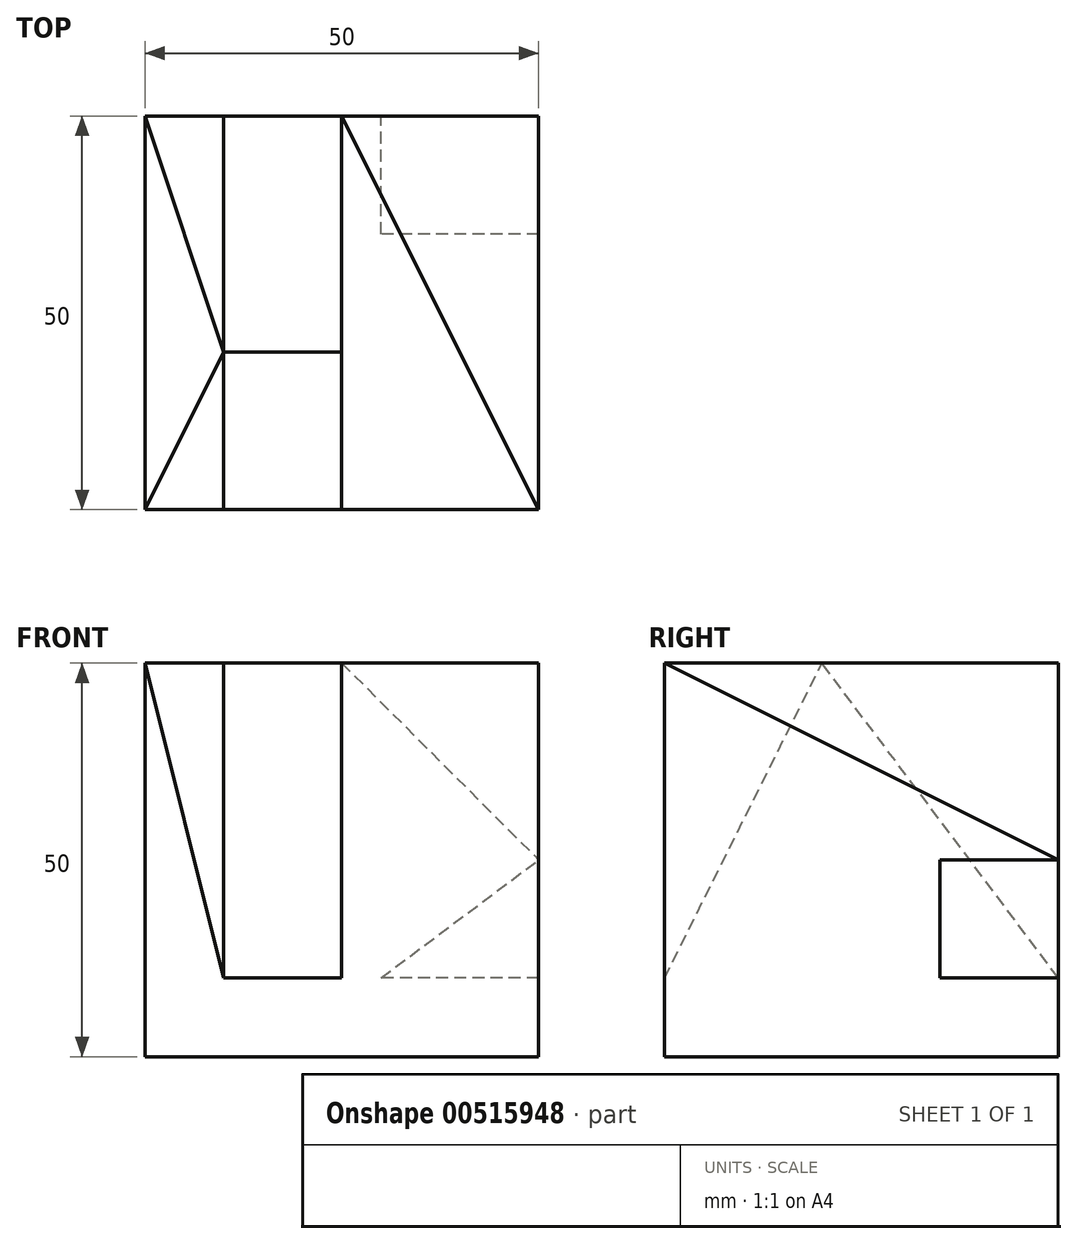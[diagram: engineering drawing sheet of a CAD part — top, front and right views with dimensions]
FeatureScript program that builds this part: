
annotation { "Feature Type Name" : "Feature", "Feature Type Description" : "" }
export const myFeature = defineFeature(function(context is Context, id is Id, definition is map)
    precondition{}
    {
        {
            var Q0;
            Q0=qCreatedBy(makeId("Top.planeOp"),FACE);
            var sketch = newSketch(context, id + "F0", { "sketchPlane" : qUnion([Q0])});
            skLineSegment(sketch, "E0.bottom", {"start": v(0, 0) * mm, "end": v(50, 0) * mm});
            skLineSegment(sketch, "E0.top", {"start": v(0, 50) * mm, "end": v(50, 50) * mm});
            skLineSegment(sketch, "E0.left", {"start": v(0, 0) * mm, "end": v(0, 50) * mm});
            skLineSegment(sketch, "E0.right", {"start": v(50, 0) * mm, "end": v(50, 50) * mm});
            skSolve(sketch);
        }
        {
            var Q0;
            Q0 = qSketchRegion(id + "F0", true);
            extrude(context, id + "F1", {"entities" : qUnion([Q0]), "depth" : 50 * mm, "offsetDistance" : 25 * mm});
        }
        {
            var Q0;
            Q0=makeQuery(id+"F1.opExtrude","CAP_FACE",FACE,{"disambiguationData":[OSD([sQuery(id+"F0.wireOp",EDGE,"E0.bottom"),sQuery(id+"F0.wireOp",EDGE,"E0.top"),sQuery(id+"F0.wireOp",EDGE,"E0.left"),sQuery(id+"F0.wireOp",EDGE,"E0.right")])],"isStart":false});
            var sketch = newSketch(context, id + "F2", { "sketchPlane" : qUnion([Q0])});
            skLineSegment(sketch, "E1", {"start": v(50, 0) * mm, "end": v(25, 50) * mm});
            skSolve(sketch);
        }
        {
            var Q0;
            Q0=makeQuery(id+"F1.opExtrude","SWEPT_FACE",FACE,{"disambiguationData":[OSD([sQuery(id+"F0.wireOp",EDGE,"E0.top")])]});
            var sketch = newSketch(context, id + "F3", { "sketchPlane" : qUnion([Q0])});
            skLineSegment(sketch, "E2", {"start": v(-25, 50) * mm, "end": v(-50, 25) * mm});
            skSolve(sketch);
        }
        {
            var Q1;
            {var subQ0=sQuery(id+"F2.wireOp",EDGE,"E1");Q1=makeQuery(id+"F2.imprint","IMPRINT",FACE,{"disambiguationData":[TD([[makeQuery(id+"F2.imprint","IMPRINT",EDGE,{"derivedFrom":subQ0}),-1.0]])]});}
            var Q2;
            Q2=sQuery(id+"F3.wireOp",VERTEX,"E2.end");
            loft(context, id + "F4", {"operationType" : NewBodyOperationType.REMOVE, "sheetProfilesArray" : [{ "sheetProfileEntities" : qUnion([Q1]) }, { "sheetProfileEntities" : qUnion([Q2]) }]});
        }
        {
            var Q0;
            Q0=makeQuery(id+"F1.opExtrude","SWEPT_FACE",FACE,{"disambiguationData":[OSD([sQuery(id+"F0.wireOp",EDGE,"E0.top")])]});
            var sketch = newSketch(context, id + "F5", { "sketchPlane" : qUnion([Q0])});
            skLineSegment(sketch, "E3", {"start": v(-50, 10) * mm, "end": v(-30, 10) * mm});
            skLineSegment(sketch, "E4", {"start": v(-30, 10) * mm, "end": v(-50, 25) * mm});
            skSolve(sketch);
        }
        {
            var Q0;
            {var subQ0=sQuery(id+"F5.wireOp",EDGE,"E3");Q0=makeQuery(id+"F5.imprint","IMPRINT",FACE,{"disambiguationData":[TD([[makeQuery(id+"F5.imprint","IMPRINT",EDGE,{"derivedFrom":subQ0}),1.0]])]});}
            extrude(context, id + "F6", {"entities" : qUnion([Q0]), "operationType" : NewBodyOperationType.REMOVE, "oppositeDirection" : true, "depth" : 15 * mm, "offsetDistance" : 25 * mm});
        }
        {
            var Q0;
            Q0=qCreatedBy(makeId("Right.planeOp"),FACE);
            cPlane(context, id + "F7", {"entities" : qUnion([Q0]), "cplaneType" : CPlaneType.OFFSET, "offset" : 10 * mm, "width" : 150 * mm, "height" : 150 * mm});
        }
        {
            var Q0;
            Q0=makeQuery(id+"F1.opExtrude","SWEPT_FACE",FACE,{"disambiguationData":[OSD([sQuery(id+"F0.wireOp",EDGE,"E0.bottom")])]});
            var sketch = newSketch(context, id + "F8", { "sketchPlane" : qUnion([Q0])});
            skLineSegment(sketch, "E5", {"start": v(0, 10) * mm, "end": v(50, 10) * mm});
            skSolve(sketch);
        }
        {
            var Q0;
            Q0=makeQuery(id+"F1.opExtrude","CAP_FACE",FACE,{"disambiguationData":[OSD([sQuery(id+"F0.wireOp",EDGE,"E0.bottom"),sQuery(id+"F0.wireOp",EDGE,"E0.top"),sQuery(id+"F0.wireOp",EDGE,"E0.left"),sQuery(id+"F0.wireOp",EDGE,"E0.right")])],"isStart":false});
            var sketch = newSketch(context, id + "F9", { "sketchPlane" : qUnion([Q0])});
            skLineSegment(sketch, "E6", {"start": v(25, 50) * mm, "end": v(25, 0) * mm});
            skLineSegment(sketch, "E7", {"start": v(25, 0) * mm, "end": v(10, 0) * mm});
            skLineSegment(sketch, "E8", {"start": v(10, 0) * mm, "end": v(10, 50) * mm});
            skLineSegment(sketch, "E9", {"start": v(10, 50) * mm, "end": v(25, 50) * mm});
            skLineSegment(sketch, "E10", {"start": v(10, 20) * mm, "end": v(25, 20) * mm});
            skSolve(sketch);
        }
        {
            var Q0;
            Q0=sQuery(id+"F8.wireOp",EDGE,"E5");
            cPoint(context, id + "F10", {"entities" : qUnion([Q0]), "parameter" : 0.5});
        }
        {
            var Q0;
            Q0=sQuery(id+"F9.wireOp",VERTEX,"E10.start");
            var Q1;
            Q1=sQuery(id+"F9.wireOp",VERTEX,"E10.end");
            var Q2;
            Q2 = qCreatedBy(id + "F10" ,VERTEX);
            cPlane(context, id + "F11", {"entities" : qUnion([Q0, Q1, Q2]), "cplaneType" : CPlaneType.THREE_POINT, "offset" : 25 * mm, "width" : 150 * mm, "height" : 150 * mm});
        }
        {
            var Q0;
            Q0=sQuery(id+"F9.wireOp",VERTEX,"E10.end");
            var Q1;
            Q1=sQuery(id+"F9.wireOp",VERTEX,"E10.start");
            var Q2;
            Q2=makeQuery(id+"F6.boolean.opBoolean","COPY",VERTEX,{"derivedFrom":makeQuery(id+"F6.opExtrude","CAP_VERTEX",VERTEX,{"disambiguationData":[OSD([sQuery(id+"F5.wireOp",EDGE,"E3"),sQuery(id+"F5.wireOp",EDGE,"E4")])],"isStart":true})});
            cPlane(context, id + "F12", {"entities" : qUnion([Q0, Q1, Q2]), "cplaneType" : CPlaneType.THREE_POINT, "offset" : 25 * mm, "width" : 150 * mm, "height" : 150 * mm});
        }
        {
            var Q0;
            {var subQ0=sQuery(id+"F9.wireOp",EDGE,"E7");Q0=makeQuery(id+"F9.imprint","IMPRINT",FACE,{"disambiguationData":[TD([[makeQuery(id+"F9.imprint","IMPRINT",EDGE,{"derivedFrom":subQ0}),1.0]])]});}
            var Q1;
            Q1=qCreatedBy(id+"F11.planeOp",FACE);
            extrude(context, id + "F13", {"entities" : qUnion([Q0]), "operationType" : NewBodyOperationType.REMOVE, "endBound" : BoundingType.UP_TO_SURFACE, "oppositeDirection" : true, "depth" : 25 * mm, "endBoundEntityFace" : qUnion([Q1]), "offsetDistance" : 25 * mm});
        }
        {
            var Q0;
            {var subQ0=sQuery(id+"F9.wireOp",EDGE,"E9");Q0=makeQuery(id+"F9.imprint","IMPRINT",FACE,{"disambiguationData":[TD([[makeQuery(id+"F9.imprint","IMPRINT",EDGE,{"derivedFrom":subQ0}),-1.0]])]});}
            var Q1;
            Q1=qCreatedBy(id+"F12.planeOp",FACE);
            extrude(context, id + "F14", {"entities" : qUnion([Q0]), "operationType" : NewBodyOperationType.REMOVE, "endBound" : BoundingType.UP_TO_SURFACE, "oppositeDirection" : true, "depth" : 25 * mm, "endBoundEntityFace" : qUnion([Q1]), "offsetDistance" : 25 * mm});
        }
        {
            var Q1;
            Q1=makeQuery(id+"F13.boolean.opBoolean","COPY",FACE,{"derivedFrom":makeQuery(id+"F13.opExtrude","SWEPT_FACE",FACE,{"disambiguationData":[OSD([sQuery(id+"F9.wireOp",EDGE,"E8")])]})});
            var Q2;
            Q2=makeQuery(id+"F1.opExtrude","CAP_VERTEX",VERTEX,{"disambiguationData":[OSD([sQuery(id+"F0.wireOp",EDGE,"E0.bottom"),sQuery(id+"F0.wireOp",EDGE,"E0.left")])],"isStart":false});
            loft(context, id + "F15", {"operationType" : NewBodyOperationType.REMOVE, "sheetProfilesArray" : [{ "sheetProfileEntities" : qUnion([Q1]) }, { "sheetProfileEntities" : qUnion([Q2]) }]});
        }
        {
            var Q1;
            Q1=makeQuery(id+"F14.boolean.opBoolean","COPY",FACE,{"derivedFrom":makeQuery(id+"F14.opExtrude","SWEPT_FACE",FACE,{"disambiguationData":[OSD([sQuery(id+"F9.wireOp",EDGE,"E8")])]})});
            var Q2;
            Q2=makeQuery(id+"F1.opExtrude","CAP_VERTEX",VERTEX,{"disambiguationData":[OSD([sQuery(id+"F0.wireOp",EDGE,"E0.top"),sQuery(id+"F0.wireOp",EDGE,"E0.left")])],"isStart":false});
            loft(context, id + "F16", {"operationType" : NewBodyOperationType.REMOVE, "sheetProfilesArray" : [{ "sheetProfileEntities" : qUnion([Q1]) }, { "sheetProfileEntities" : qUnion([Q2]) }]});
        }
    });
